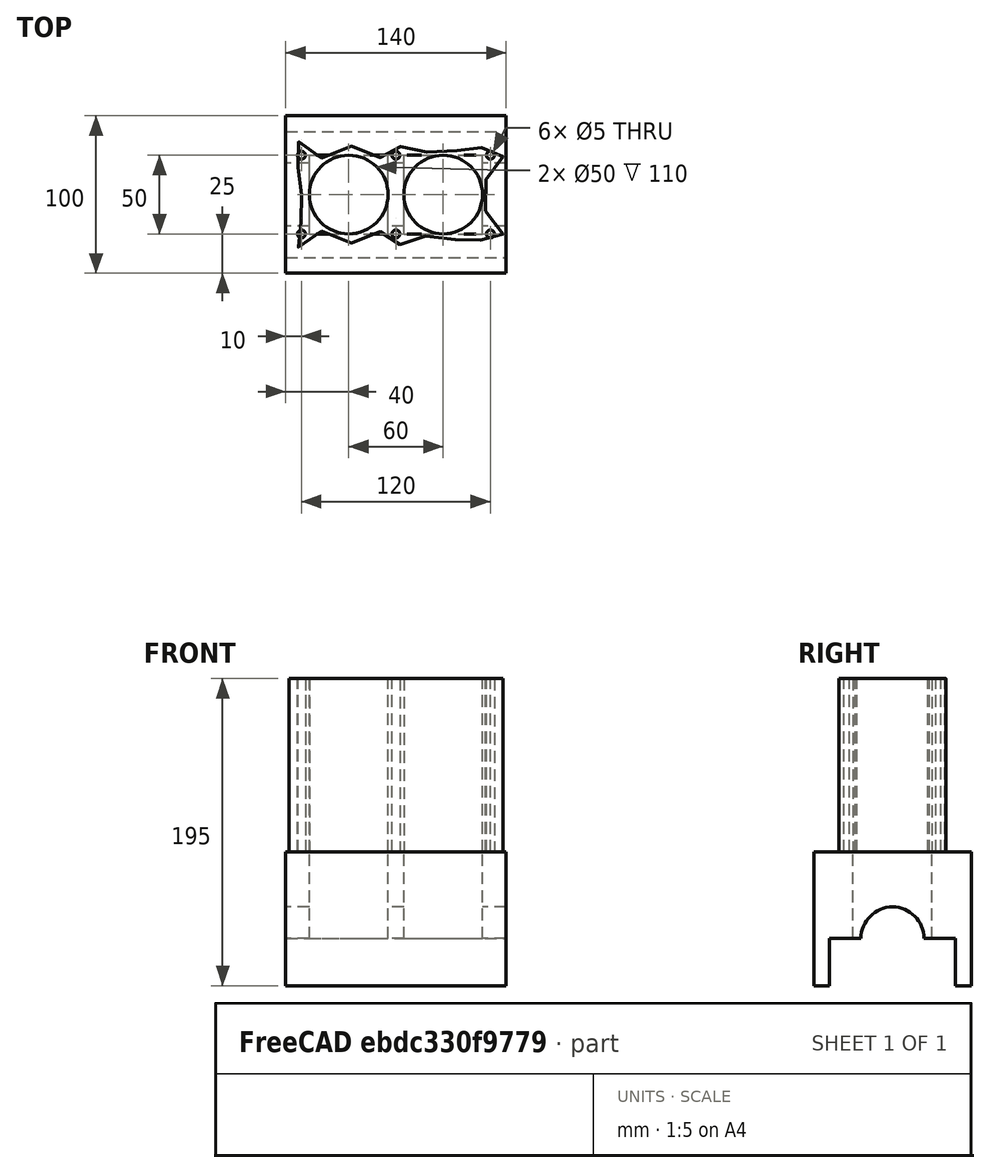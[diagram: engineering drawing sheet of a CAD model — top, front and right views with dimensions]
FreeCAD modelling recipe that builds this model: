
FCSTD DOCUMENT  (FreeCAD 1.0R39285 (Git))
Label: EngineBlock
License: Creative Commons Attribution-ShareAlike
LicenseURL: https://creativecommons.org/licenses/by-sa/4.0/
objects: Part::Part2DObjectPython×8, Part::Extrusion×7, Part::Box×5, Part::Cut×5, Part::Cylinder×3, Part::MultiFuse×3, Part::Mirroring×3, App::DocumentObjectGroup×1, Part::MultiCommon×1
note: 35 computed .brp shape members not serialized (recipe doc carries the construction recipe); baked Part::Feature solids carry a one-line shape summary decoded from their .brp

FEATURE [Part::Box] Box  label="Billet"
  AttacherType = Attacher::AttachEngine3D
  Height = 110
  Length = 140
  Placement = pos=(0,-40,0) rot=(0,0,1;0rad)
  Width = 80
FEATURE [Part::Cylinder] Cylinder  label="Cylinder 1"
  Angle = 360
  AttacherType = Attacher::AttachEngine3D
  FirstAngle = 0
  Height = 110
  Placement = pos=(40,0,0) rot=(0,0,1;0rad)
  Radius = 25
  SecondAngle = 0
FEATURE [Part::Cylinder] Cylinder001  label="Cylinder 2"
  Angle = 360
  AttacherType = Attacher::AttachEngine3D
  FirstAngle = 0
  Height = 110
  Placement = pos=(100,0,0) rot=(0,0,1;0rad)
  Radius = 25
  SecondAngle = 0
FEATURE [Part::MultiFuse] Fusion  label="Cylinders"
  Shapes = -> [Cylinder,Cylinder001]
FEATURE [Part::Cut] Cut  label="Bored Block"
  Base = -> Box
  Tool = -> Fusion
FEATURE [Part::Box] Box001  label="Crankcase Billet"
  AttacherType = Attacher::AttachEngine3D
  Height = 85
  Length = 140
  Placement = pos=(0,-50,-85) rot=(0,0,1;0rad)
  Width = 100
FEATURE [Part::Box] Box002  label="Bearing carve"
  AttacherType = Attacher::AttachEngine3D
  Height = 30
  Length = 140
  Placement = pos=(0,-40,-85) rot=(0,0,1;0rad)
  Width = 80
FEATURE [Part::Cut] Cut001  label="Carved crankcase"
  Base = -> Box001
  Tool = -> Box002
FEATURE [Part::Cylinder] Cylinder002  label="Cranshaft carve"
  Angle = 360
  AttacherType = Attacher::AttachEngine3D
  FirstAngle = 0
  Height = 140
  Placement = pos=(0,0,-55) rot=(0,1,0;1.5708rad)
  Radius = 20
  SecondAngle = 0
FEATURE [Part::Cut] Cut002  label="Crankcase with journals"
  Base = -> Cut001
  Tool = -> Cylinder002
FEATURE [Part::Box] Box003  label="Box carve 1"
  AttacherType = Attacher::AttachEngine3D
  Height = 55
  Length = 50
  Placement = pos=(15,-25,-55) rot=(0,0,1;0rad)
  Width = 50
FEATURE [Part::Box] Box004  label="Box carve 2"
  AttacherType = Attacher::AttachEngine3D
  Height = 55
  Length = 50
  Placement = pos=(75,-25,-55) rot=(0,0,1;0rad)
  Width = 50
FEATURE [Part::MultiFuse] Fusion001  label="Box carvers"
  Shapes = -> [Box003,Box004]
FEATURE [Part::Cut] Cut003  label="Crankcase"
  Base = -> Cut002
  Tool = -> Fusion001
FEATURE [Part::Part2DObjectPython] Circle003  label="Bolt 007"  # Draft 2D object (typed FeaturePython)
  FirstAngle = 0
  LastAngle = 0
  MapMode = 5
  Placement = pos=(10,25,110) rot=(0,0,1;0rad)
  Radius = 2.5
FEATURE [Part::Mirroring] Part__Mirroring  label="Bolt 4"
  Base = (0,0,0)
  Normal = (0,1,0)
  Source = -> Circle003
FEATURE [Part::Extrusion] Extrude  label="Head bolt bore 1"
  Base = -> Circle003
  Dir = (0,0,-110)
  DirMode = 0
  FaceMakerClass = Part::FaceMakerExtrusion
  FaceMakerMode = 2
  LengthFwd = 0
  LengthRev = 0
  Solid = false
  Symmetric = false
FEATURE [Part::Extrusion] Extrude003  label="Head bolt bore 4"
  Base = -> Part__Mirroring
  Dir = (0,0,-110)
  DirMode = 0
  FaceMakerClass = Part::FaceMakerExtrusion
  FaceMakerMode = 2
  LengthFwd = 0
  LengthRev = 0
  Solid = false
  Symmetric = false
FEATURE [Part::Part2DObjectPython] Circle004  label="Bolt 008"  # Draft 2D object (typed FeaturePython)
  FirstAngle = 0
  LastAngle = 0
  MapMode = 5
  Placement = pos=(70,25,110) rot=(0,0,1;0rad)
  Radius = 2.5
FEATURE [Part::Mirroring] Part__Mirroring001  label="Bolt 5"
  Base = (0,0,0)
  Normal = (0,1,0)
  Source = -> Circle004
FEATURE [Part::Extrusion] Extrude001  label="Head bolt bore 2"
  Base = -> Circle004
  Dir = (0,0,-110)
  DirMode = 0
  FaceMakerClass = Part::FaceMakerExtrusion
  FaceMakerMode = 2
  LengthFwd = 0
  LengthRev = 0
  Solid = false
  Symmetric = false
FEATURE [Part::Extrusion] Extrude004  label="Head bolt bore 5"
  Base = -> Part__Mirroring001
  Dir = (0,0,-110)
  DirMode = 0
  FaceMakerClass = Part::FaceMakerExtrusion
  FaceMakerMode = 2
  LengthFwd = 0
  LengthRev = 0
  Solid = false
  Symmetric = false
FEATURE [Part::Part2DObjectPython] Circle005  label="Bolt 009"  # Draft 2D object (typed FeaturePython)
  FirstAngle = 0
  LastAngle = 0
  MapMode = 5
  Placement = pos=(130,25,110) rot=(0,0,1;0rad)
  Radius = 2.5
FEATURE [Part::Mirroring] Part__Mirroring002  label="Bolt 6"
  Base = (0,0,0)
  Normal = (0,1,0)
  Source = -> Circle005
FEATURE [Part::Extrusion] Extrude002  label="Head bolt bore 3"
  Base = -> Circle005
  Dir = (0,0,-110)
  DirMode = 0
  FaceMakerClass = Part::FaceMakerExtrusion
  FaceMakerMode = 2
  LengthFwd = 0
  LengthRev = 0
  Solid = false
  Symmetric = false
FEATURE [Part::Extrusion] Extrude005  label="Head bolt bore 6"
  Base = -> Part__Mirroring002
  Dir = (0,0,-110)
  DirMode = 0
  FaceMakerClass = Part::FaceMakerExtrusion
  FaceMakerMode = 2
  LengthFwd = 0
  LengthRev = 0
  Solid = false
  Symmetric = false
FEATURE [Part::MultiFuse] Fusion002  label="Head bolt boreholes"
  Shapes = -> [Extrude,Extrude001,Extrude002,Extrude003,Extrude004,Extrude005]
FEATURE [Part::Cut] Cut004  label="Block with headbolts"
  Base = -> Cut
  Tool = -> Fusion002
FEATURE [Part::Part2DObjectPython] Polygon004  # Draft 2D object (typed FeaturePython)
  ChamferSize = 0
  DrawMode = 0
  FacesNumber = 14
  FilletRadius = 0
  MapMode = 5
  Placement = pos=(40,0,110) rot=(0,0,1;0rad)
  Radius = 30
FEATURE [Part::Part2DObjectPython] Polygon005  # Draft 2D object (typed FeaturePython)
  ChamferSize = 0
  DrawMode = 0
  FacesNumber = 14
  FilletRadius = 0
  MapMode = 5
  Placement = pos=(100,0,110) rot=(0,0,1;0rad)
  Radius = 30
FEATURE [Part::Part2DObjectPython] Polygon006  # Draft 2D object (typed FeaturePython)
  ChamferSize = 0
  DrawMode = 0
  FacesNumber = 22
  FilletRadius = 0
  MapMode = 5
  Placement = pos=(40,0,110) rot=(0,0,1;0rad)
  Radius = 45
FEATURE [Part::Part2DObjectPython] Polygon007  # Draft 2D object (typed FeaturePython)
  ChamferSize = 0
  DrawMode = 0
  FacesNumber = 22
  FilletRadius = 0
  MapMode = 5
  Placement = pos=(100,0,110) rot=(0,0,1;0rad)
  Radius = 45
FEATURE [App::DocumentObjectGroup] Construction
  Group = -> [Polygon004,Polygon005,Polygon006,Polygon007]
FEATURE [Part::Part2DObjectPython] BSpline001  # Draft 2D object (typed FeaturePython)
  Closed = true
  MapMode = 5
  Parameterization = 1
  Points = (36) [(10,2.75536e-15,110),(12.9709,13.0165,110),(2.14359,24.3288,110),(10.5313,34.0087,110),(21.2953,23.4549,110),(33.3244,29.2478,110),+30 more]
FEATURE [Part::Extrusion] Extrude006  label="Extruded spline"
  Base = -> BSpline001
  Dir = (0,0,-110)
  DirMode = 0
  FaceMakerClass = Part::FaceMakerExtrusion
  FaceMakerMode = 2
  LengthFwd = 0
  LengthRev = 0
  Solid = false
  Symmetric = false
FEATURE [Part::MultiCommon] Common  label="Engine block"
  Shapes = -> [Extrude006,Cut004]
